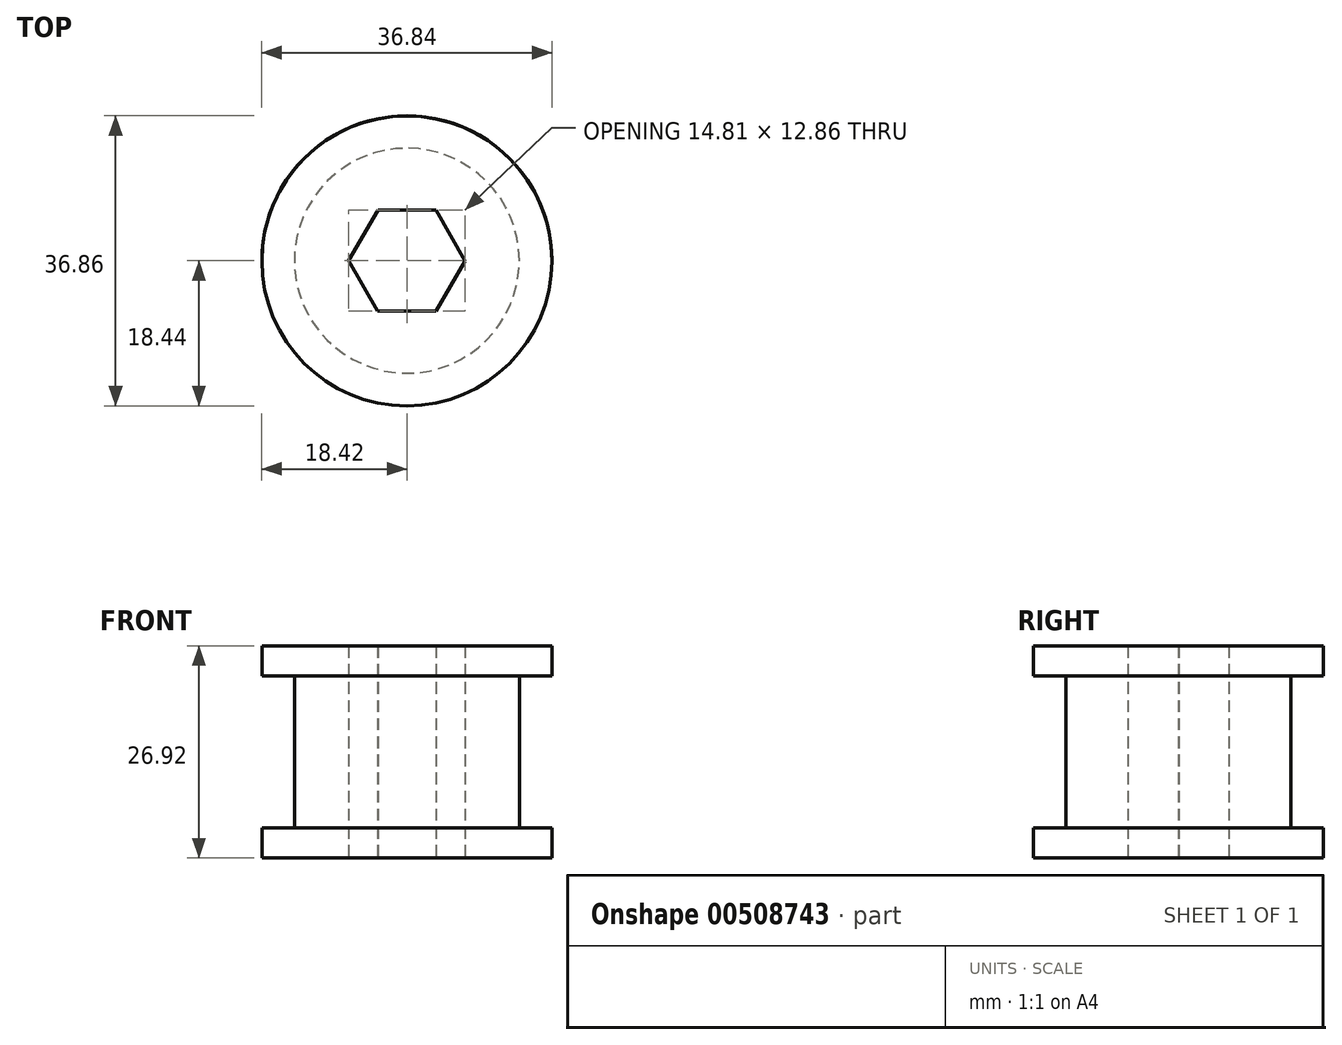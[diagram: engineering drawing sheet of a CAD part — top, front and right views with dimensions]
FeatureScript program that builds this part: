
annotation { "Feature Type Name" : "Feature", "Feature Type Description" : "" }
export const myFeature = defineFeature(function(context is Context, id is Id, definition is map)
    precondition{}
    {
        {
            var Q0;
            Q0=qCreatedBy(makeId("Top.planeOp"),FACE);
            var sketch = newSketch(context, id + "F0", { "sketchPlane" : qUnion([Q0])});
            skCircle(sketch, "E0.cCircle", {"center": v(0, 0) * mm, "radius": 6.41 * mm, "construction": true});
            skLineSegment(sketch, "E0.0", {"start": v(3.73, 6.4) * mm, "end": v(7.4, -0.03) * mm});
            skLineSegment(sketch, "E0.1", {"start": v(7.4, -0.03) * mm, "end": v(3.68, -6.43) * mm});
            skLineSegment(sketch, "E0.2", {"start": v(3.68, -6.43) * mm, "end": v(-3.73, -6.4) * mm});
            skLineSegment(sketch, "E0.3", {"start": v(-3.73, -6.4) * mm, "end": v(-7.4, 0.03) * mm});
            skLineSegment(sketch, "E0.4", {"start": v(-7.4, 0.03) * mm, "end": v(-3.68, 6.43) * mm});
            skLineSegment(sketch, "E0.5", {"start": v(-3.68, 6.43) * mm, "end": v(3.73, 6.4) * mm});
            skPoint(sketch, "E0.0.midPoint", {"position": v(5.57, 3.19) * mm});
            skCircle(sketch, "E1", {"center": v(0, 0) * mm, "radius": 14.29 * mm});
            skSolve(sketch);
        }
        {
            var Q0;
            Q0=makeQuery(id+"F0.imprint","IMPRINT",FACE,{"disambiguationData":[TD([[makeQuery(id+"F0.imprint","IMPRINT",EDGE,{"derivedFrom":sQuery(id+"F0.wireOp",EDGE,"E0.0")}),1.0]])]});
            extrude(context, id + "F1", {"entities" : qUnion([Q0]), "depth" : 19.3 * mm});
        }
        {
            var Q0;
            Q0=makeQuery(id+"F1.opExtrude","CAP_FACE",FACE,{"disambiguationData":[OSD([sQuery(id+"F0.wireOp",EDGE,"E0.0"),sQuery(id+"F0.wireOp",EDGE,"E0.1"),sQuery(id+"F0.wireOp",EDGE,"E0.2"),sQuery(id+"F0.wireOp",EDGE,"E0.3"),sQuery(id+"F0.wireOp",EDGE,"E0.4"),sQuery(id+"F0.wireOp",EDGE,"E0.5"),sQuery(id+"F0.wireOp",EDGE,"E1")])],"isStart":false});
            var sketch = newSketch(context, id + "F2", { "sketchPlane" : qUnion([Q0])});
            skCircle(sketch, "E2", {"center": v(0, -0.03) * mm, "radius": 18.41 * mm});
            skCircle(sketch, "E3.cCircle", {"center": v(0, 0) * mm, "radius": 6.41 * mm, "construction": true});
            skLineSegment(sketch, "E3.0", {"start": v(3.73, 6.4) * mm, "end": v(7.4, -0.03) * mm});
            skLineSegment(sketch, "E3.1", {"start": v(7.4, -0.03) * mm, "end": v(3.68, -6.43) * mm});
            skLineSegment(sketch, "E3.2", {"start": v(3.68, -6.43) * mm, "end": v(-3.73, -6.4) * mm});
            skLineSegment(sketch, "E3.3", {"start": v(-3.73, -6.4) * mm, "end": v(-7.4, 0.03) * mm});
            skLineSegment(sketch, "E3.4", {"start": v(-7.4, 0.03) * mm, "end": v(-3.68, 6.43) * mm});
            skLineSegment(sketch, "E3.5", {"start": v(-3.68, 6.43) * mm, "end": v(3.73, 6.4) * mm});
            skPoint(sketch, "E3.0.midPoint", {"position": v(5.57, 3.19) * mm});
            skSolve(sketch);
        }
        {
            var Q0;
            Q0 = qSketchRegion(id + "F2", true);
            extrude(context, id + "F3", {"entities" : qUnion([Q0]), "operationType" : NewBodyOperationType.ADD, "depth" : 3.8 * mm});
        }
        {
            var Q0;
            Q0=makeQuery(id+"F1.opExtrude","CAP_FACE",FACE,{"disambiguationData":[OSD([sQuery(id+"F0.wireOp",EDGE,"E0.0"),sQuery(id+"F0.wireOp",EDGE,"E0.1"),sQuery(id+"F0.wireOp",EDGE,"E0.2"),sQuery(id+"F0.wireOp",EDGE,"E0.3"),sQuery(id+"F0.wireOp",EDGE,"E0.4"),sQuery(id+"F0.wireOp",EDGE,"E0.5"),sQuery(id+"F0.wireOp",EDGE,"E1")])],"isStart":true});
            var sketch = newSketch(context, id + "F4", { "sketchPlane" : qUnion([Q0])});
            skCircle(sketch, "E4.cCircle", {"center": v(0, 0) * mm, "radius": 6.41 * mm, "construction": true});
            skLineSegment(sketch, "E4.0", {"start": v(7.4, 0.03) * mm, "end": v(3.73, -6.4) * mm});
            skLineSegment(sketch, "E4.1", {"start": v(3.73, -6.4) * mm, "end": v(-3.68, -6.43) * mm});
            skLineSegment(sketch, "E4.2", {"start": v(-3.68, -6.43) * mm, "end": v(-7.4, -0.03) * mm});
            skLineSegment(sketch, "E4.3", {"start": v(-7.4, -0.03) * mm, "end": v(-3.73, 6.4) * mm});
            skLineSegment(sketch, "E4.4", {"start": v(-3.73, 6.4) * mm, "end": v(3.68, 6.43) * mm});
            skLineSegment(sketch, "E4.5", {"start": v(3.68, 6.43) * mm, "end": v(7.4, 0.03) * mm});
            skPoint(sketch, "E4.0.midPoint", {"position": v(5.57, -3.19) * mm});
            skCircle(sketch, "E5", {"center": v(0, 0) * mm, "radius": 18.41 * mm});
            skSolve(sketch);
        }
        {
            var Q0;
            Q0 = qSketchRegion(id + "F4", true);
            extrude(context, id + "F5", {"entities" : qUnion([Q0]), "operationType" : NewBodyOperationType.ADD, "depth" : 3.8 * mm});
        }
    });
